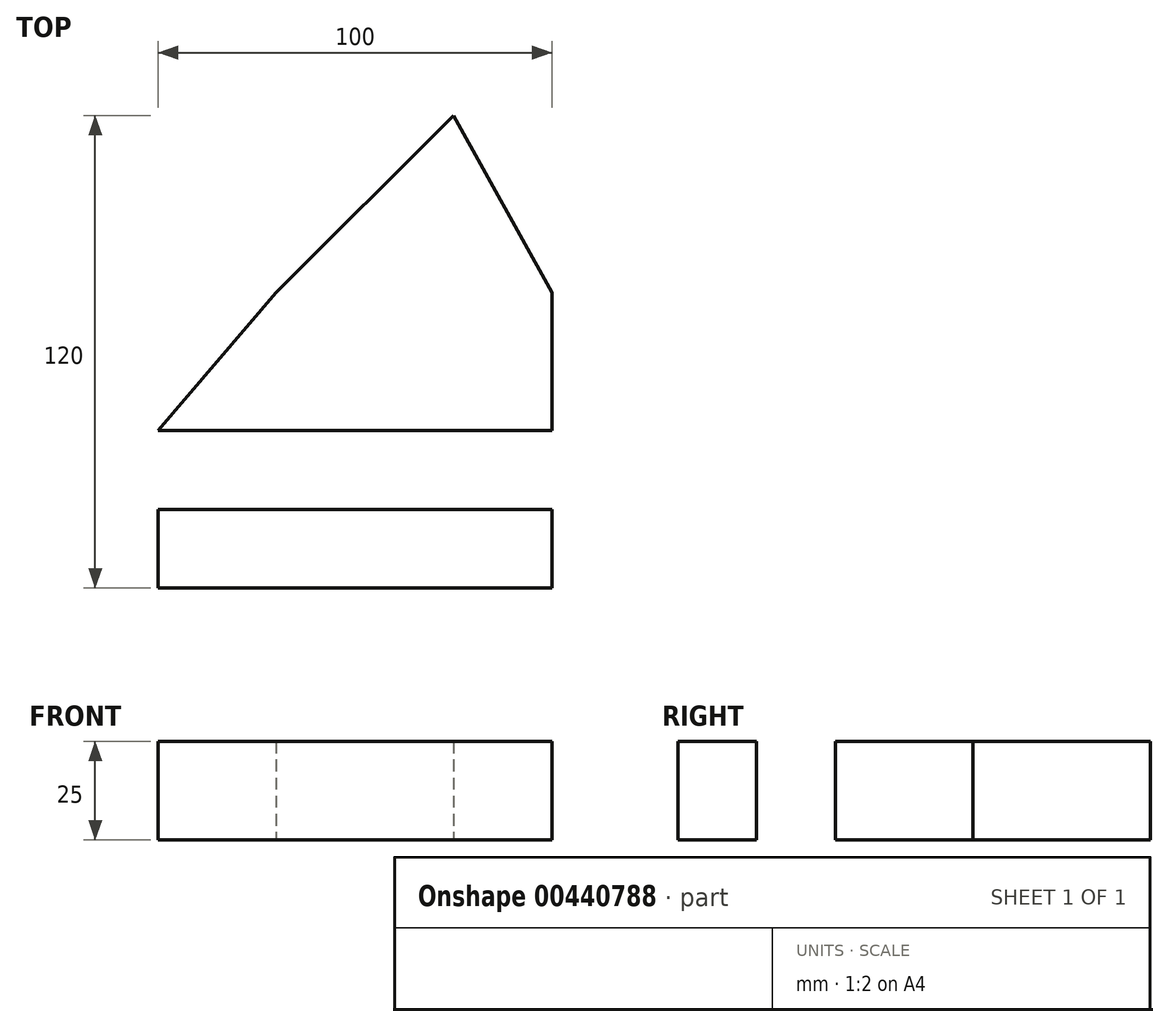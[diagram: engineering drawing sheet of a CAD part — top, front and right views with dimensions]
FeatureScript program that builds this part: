
annotation { "Feature Type Name" : "Feature", "Feature Type Description" : "" }
export const myFeature = defineFeature(function(context is Context, id is Id, definition is map)
    precondition{}
    {
        {
            var Q0;
            Q0=qCreatedBy(makeId("Top.planeOp"),FACE);
            var sketch = newSketch(context, id + "F0", { "sketchPlane" : qUnion([Q0])});
            skLineSegment(sketch, "E0.bottom", {"start": v(-73.94, 31.13) * mm, "end": v(26.06, 31.13) * mm});
            skLineSegment(sketch, "E0.top", {"start": v(-73.94, 11.13) * mm, "end": v(26.06, 11.13) * mm});
            skLineSegment(sketch, "E0.left", {"start": v(-73.94, 31.13) * mm, "end": v(-73.94, 11.13) * mm});
            skLineSegment(sketch, "E0.right", {"start": v(26.06, 31.13) * mm, "end": v(26.06, 11.13) * mm});
            skLineSegment(sketch, "E1.top", {"start": v(-73.94, 51.13) * mm, "end": v(26.06, 51.13) * mm});
            skLineSegment(sketch, "E1.left", {"start": v(-73.94, 31.13) * mm, "end": v(-73.94, 51.13) * mm});
            skLineSegment(sketch, "E1.right", {"start": v(26.06, 31.13) * mm, "end": v(26.06, 51.13) * mm});
            skLineSegment(sketch, "E2", {"start": v(-73.94, 51.13) * mm, "end": v(-43.94, 86.13) * mm});
            skLineSegment(sketch, "E3", {"start": v(-43.94, 86.13) * mm, "end": v(26.06, 86.13) * mm});
            skLineSegment(sketch, "E4", {"start": v(26.06, 86.13) * mm, "end": v(26.06, 51.13) * mm});
            skLineSegment(sketch, "E5", {"start": v(-43.94, 86.13) * mm, "end": v(1.06, 131.13) * mm});
            skLineSegment(sketch, "E6", {"start": v(26.06, 86.13) * mm, "end": v(1.06, 131.13) * mm});
            skSolve(sketch);
        }
        {
            var Q0;
            Q0=makeQuery(id+"F0.imprint","IMPRINT",FACE,{"disambiguationData":[TD([[makeQuery(id+"F0.imprint","IMPRINT",EDGE,{"derivedFrom":sQuery(id+"F0.wireOp",EDGE,"E3")}),1.0]])]});
            var Q1;
            Q1=makeQuery(id+"F0.imprint","IMPRINT",FACE,{"disambiguationData":[TD([[makeQuery(id+"F0.imprint","IMPRINT",EDGE,{"derivedFrom":sQuery(id+"F0.wireOp",EDGE,"E1.top")}),1.0]])]});
            var Q2;
            Q2=makeQuery(id+"F0.imprint","IMPRINT",FACE,{"disambiguationData":[TD([[makeQuery(id+"F0.imprint","IMPRINT",EDGE,{"derivedFrom":sQuery(id+"F0.wireOp",EDGE,"E0.bottom")}),1.0]])]});
            var Q3;
            Q3=makeQuery(id+"F0.imprint","IMPRINT",FACE,{"disambiguationData":[TD([[makeQuery(id+"F0.imprint","IMPRINT",EDGE,{"derivedFrom":sQuery(id+"F0.wireOp",EDGE,"E0.top")}),1.0]])]});
            extrude(context, id + "F1", {"entities" : qUnion([Q0, Q1, Q2, Q3]), "depth" : 25 * mm});
        }
    });
